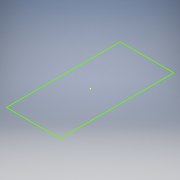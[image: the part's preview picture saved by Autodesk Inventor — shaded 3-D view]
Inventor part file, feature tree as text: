
AUTODESK INVENTOR PART (.ipt)
format: ipt  version: 2019 (Build 230136000, 136)  size: 83,456 bytes
history: native  units: in
note: dims shown in document units (in); Inventor stores cm internally (conversion verified against a paired STEP export)
features: sketch x1
ambient origin geometry x8: Origin, YZ Plane, XZ Plane, XY Plane, X Axis, Y Axis, Z Axis, Center Point
feature tree (1):
  sketch  "Sketch1"
